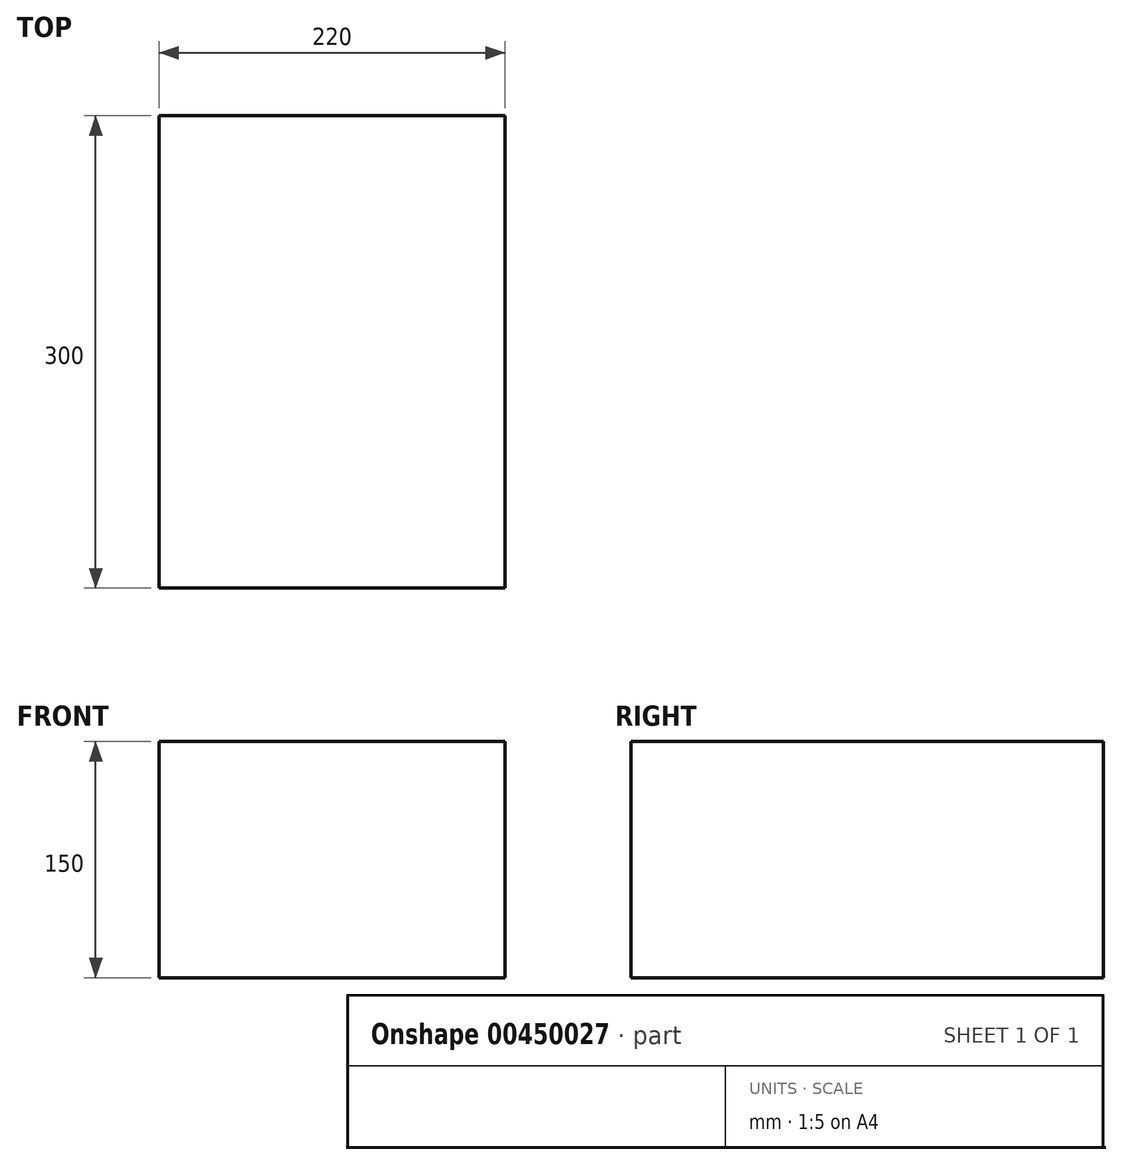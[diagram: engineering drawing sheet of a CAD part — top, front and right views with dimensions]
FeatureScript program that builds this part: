
annotation { "Feature Type Name" : "Feature", "Feature Type Description" : "" }
export const myFeature = defineFeature(function(context is Context, id is Id, definition is map)
    precondition{}
    {
        {
            var Q0;
            Q0=qCreatedBy(makeId("Top.planeOp"),FACE);
            var sketch = newSketch(context, id + "F0", { "sketchPlane" : qUnion([Q0])});
            skLineSegment(sketch, "E0.bottom", {"start": v(-110, -150) * mm, "end": v(110, -150) * mm});
            skLineSegment(sketch, "E0.top", {"start": v(-110, 150) * mm, "end": v(110, 150) * mm});
            skLineSegment(sketch, "E0.left", {"start": v(-110, -150) * mm, "end": v(-110, 150) * mm});
            skLineSegment(sketch, "E0.right", {"start": v(110, -150) * mm, "end": v(110, 150) * mm});
            skPoint(sketch, "E0.middle", {"position": v(0, 0) * mm});
            skSolve(sketch);
        }
        {
            var Q0;
            Q0=makeQuery(id+"F0.imprint","IMPRINT",FACE,{"disambiguationData":[TD([[makeQuery(id+"F0.imprint","IMPRINT",EDGE,{"derivedFrom":sQuery(id+"F0.wireOp",EDGE,"E0.bottom")}),1.0]])]});
            extrude(context, id + "F1", {"entities" : qUnion([Q0]), "depth" : 150 * mm});
        }
    });
